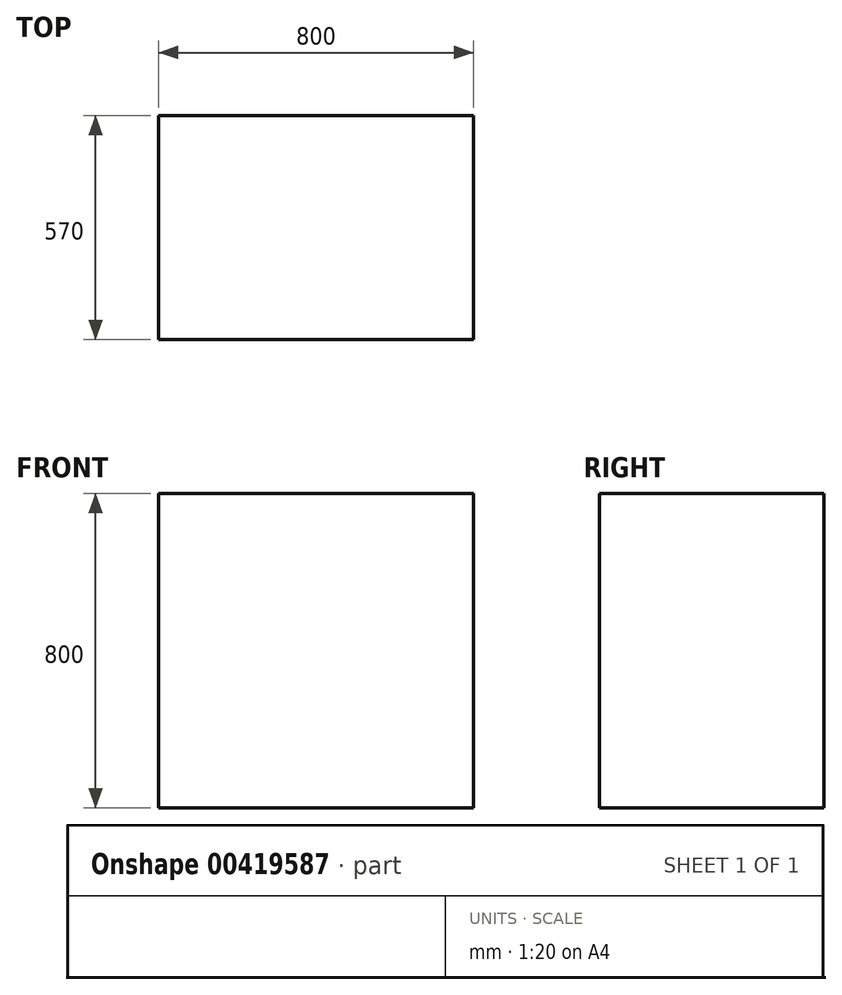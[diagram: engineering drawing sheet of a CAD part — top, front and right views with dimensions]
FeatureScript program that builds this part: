
annotation { "Feature Type Name" : "Feature", "Feature Type Description" : "" }
export const myFeature = defineFeature(function(context is Context, id is Id, definition is map)
    precondition{}
    {
        {
            var Q0;
            Q0=qCreatedBy(makeId("Top.planeOp"),FACE);
            var sketch = newSketch(context, id + "F0", { "sketchPlane" : qUnion([Q0])});
            skLineSegment(sketch, "E0.bottom", {"start": v(-674.89, 514.99) * mm, "end": v(125.11, 514.99) * mm});
            skLineSegment(sketch, "E0.top", {"start": v(-674.89, -55.01) * mm, "end": v(125.11, -55.01) * mm});
            skLineSegment(sketch, "E0.left", {"start": v(-674.89, 514.99) * mm, "end": v(-674.89, -55.01) * mm});
            skLineSegment(sketch, "E0.right", {"start": v(125.11, 514.99) * mm, "end": v(125.11, -55.01) * mm});
            skSolve(sketch);
        }
        {
            var Q0;
            Q0=makeQuery(id+"F0.imprint","IMPRINT",FACE,{"disambiguationData":[TD([[makeQuery(id+"F0.imprint","IMPRINT",EDGE,{"derivedFrom":sQuery(id+"F0.wireOp",EDGE,"E0.bottom")}),-1.0]])]});
            extrude(context, id + "F1", {"entities" : qUnion([Q0]), "depth" : 800 * mm});
        }
    });
